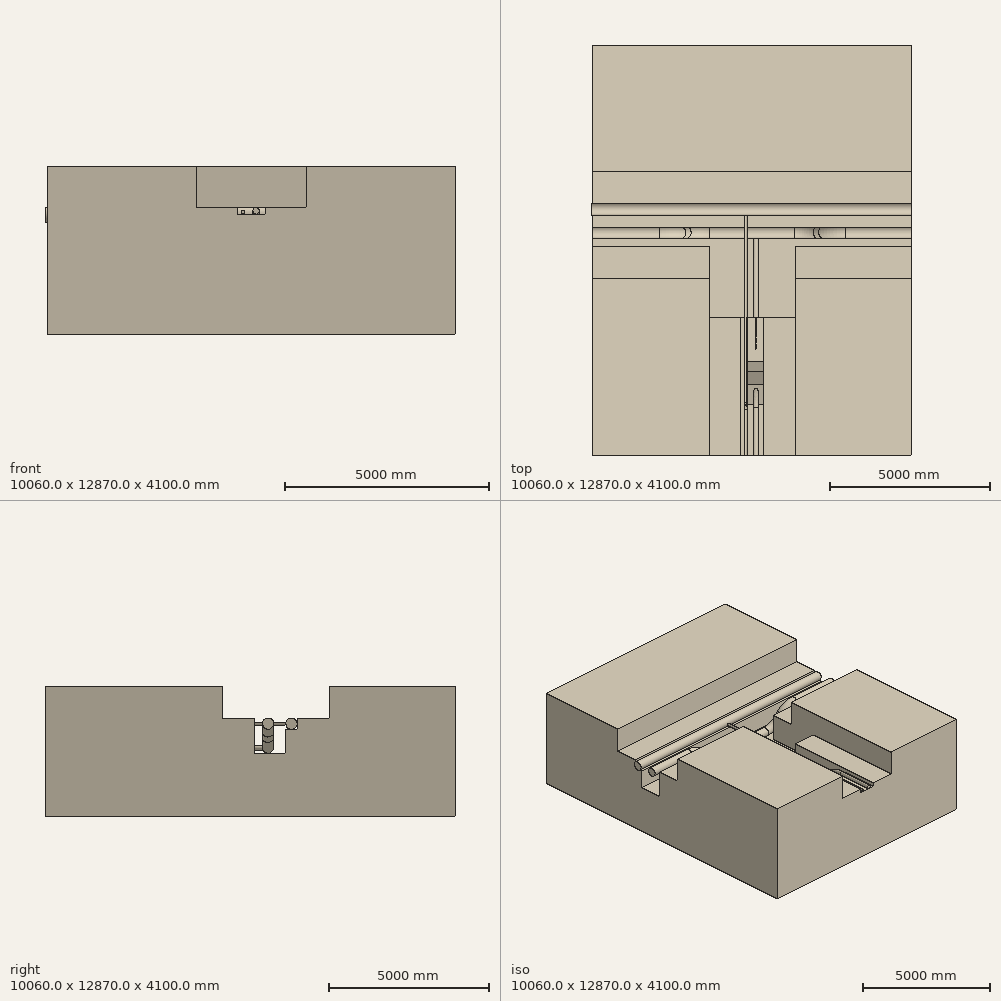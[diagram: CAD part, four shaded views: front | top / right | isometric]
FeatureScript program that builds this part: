
annotation { "Feature Type Name" : "Feature", "Feature Type Description" : "" }
export const myFeature = defineFeature(function(context is Context, id is Id, definition is map)
    precondition{}
    {
        {
            var Q0;
            Q0=qCreatedBy(makeId("Top.planeOp"),FACE);
            var sketch = newSketch(context, id + "F0", { "sketchPlane" : qUnion([Q0])});
            skLineSegment(sketch, "E0.bottom", {"start": v(-4998.89, 4864.79) * mm, "end": v(5001.11, 4864.79) * mm});
            skLineSegment(sketch, "E0.top", {"start": v(-4998.89, -4135.21) * mm, "end": v(5001.11, -4135.21) * mm});
            skLineSegment(sketch, "E0.left", {"start": v(-4998.89, 4864.79) * mm, "end": v(-4998.89, -4135.21) * mm});
            skLineSegment(sketch, "E0.right", {"start": v(5001.11, 4864.79) * mm, "end": v(5001.11, -4135.21) * mm});
            skSolve(sketch);
        }
        {
            var Q0;
            Q0 = qSketchRegion(id + "F0", true);
            extrude(context, id + "F1", {"entities" : qUnion([Q0]), "oppositeDirection" : true, "depth" : 4100 * mm});
        }
        {
            var Q0;
            Q0=makeQuery(id+"F1.opExtrude","SWEPT_FACE",FACE,{"disambiguationData":[OSD([sQuery(id+"F0.wireOp",EDGE,"E0.right")])]});
            var sketch = newSketch(context, id + "F2", { "sketchPlane" : qUnion([Q0])});
            skLineSegment(sketch, "E1", {"start": v(4764.79, 0) * mm, "end": v(4764.79, -1000) * mm});
            skLineSegment(sketch, "E2", {"start": v(4764.79, -1000) * mm, "end": v(3764.79, -1000) * mm});
            skLineSegment(sketch, "E3", {"start": v(3764.79, -1000) * mm, "end": v(3764.79, -1355) * mm});
            skLineSegment(sketch, "E4", {"start": v(3764.79, -1355) * mm, "end": v(3409.79, -1355) * mm});
            skLineSegment(sketch, "E5", {"start": v(2409.79, 0) * mm, "end": v(4764.79, 0) * mm});
            skLineSegment(sketch, "E6", {"start": v(3409.79, -1355) * mm, "end": v(3409.79, -2110) * mm});
            skLineSegment(sketch, "E7", {"start": v(3409.79, -2110) * mm, "end": v(2409.79, -2110) * mm});
            skLineSegment(sketch, "E8", {"start": v(2409.79, -2110) * mm, "end": v(2409.79, 0) * mm});
            skSolve(sketch);
        }
        {
            var Q0;
            Q0 = qSketchRegion(id + "F2", true);
            extrude(context, id + "F3", {"entities" : qUnion([Q0]), "operationType" : NewBodyOperationType.REMOVE, "endBound" : BoundingType.THROUGH_ALL, "oppositeDirection" : true, "depth" : 25 * mm});
        }
        {
            var Q0;
            Q0=makeQuery(id+"F1.opExtrude","SWEPT_FACE",FACE,{"disambiguationData":[OSD([sQuery(id+"F0.wireOp",EDGE,"E0.right")])]});
            var sketch = newSketch(context, id + "F4", { "sketchPlane" : qUnion([Q0])});
            skCircle(sketch, "E9", {"center": v(3587.29, -1177.5) * mm, "radius": 177.5 * mm});
            skSolve(sketch);
        }
        {
            var Q0;
            Q0 = qSketchRegion(id + "F4", true);
            extrude(context, id + "F5", {"entities" : qUnion([Q0]), "operationType" : NewBodyOperationType.ADD, "oppositeDirection" : true, "depth" : 10050 * mm});
        }
        {
            var Q0;
            Q0=makeQuery(id+"F1.opExtrude","SWEPT_FACE",FACE,{"disambiguationData":[OSD([sQuery(id+"F0.wireOp",EDGE,"E0.top")])]});
            var sketch = newSketch(context, id + "F6", { "sketchPlane" : qUnion([Q0])});
            skLineSegment(sketch, "E10.bottom", {"start": v(-348.89, 0) * mm, "end": v(351.11, 0) * mm});
            skLineSegment(sketch, "E10.top", {"start": v(-348.89, -1160) * mm, "end": v(351.11, -1160) * mm});
            skLineSegment(sketch, "E10.left", {"start": v(-348.89, 0) * mm, "end": v(-348.89, -1160) * mm});
            skLineSegment(sketch, "E10.right", {"start": v(351.11, 0) * mm, "end": v(351.11, -1160) * mm});
            skSolve(sketch);
        }
        {
            var Q0;
            Q0 = qSketchRegion(id + "F6", true);
            extrude(context, id + "F7", {"entities" : qUnion([Q0]), "operationType" : NewBodyOperationType.REMOVE, "endBound" : BoundingType.UP_TO_NEXT, "oppositeDirection" : true, "depth" : 25 * mm});
        }
        {
            var Q0;
            Q0=makeQuery(id+"F3.boolean.opBoolean","COPY",FACE,{"derivedFrom":makeQuery(id+"F3.opExtrude","SWEPT_FACE",FACE,{"disambiguationData":[OSD([sQuery(id+"F2.wireOp",EDGE,"E6")])]})});
            cPlane(context, id + "F8", {"entities" : qUnion([Q0]), "cplaneType" : CPlaneType.OFFSET, "offset" : 555 * mm, "width" : 150 * mm, "height" : 150 * mm});
        }
        {
            var Q0;
            Q0=qCreatedBy(id+"F8.planeOp",FACE);
            var sketch = newSketch(context, id + "F9", { "sketchPlane" : qUnion([Q0])});
            skLineSegment(sketch, "E11", {"start": v(-4998.89, -1177.5) * mm, "end": v(-2913.1, -1177.5) * mm});
            skLineSegment(sketch, "E12", {"start": v(-2206, -1470.4) * mm, "end": v(-2036.78, -1639.6) * mm});
            skLineSegment(sketch, "E13", {"start": v(-1329.67, -1932.5) * mm, "end": v(1341.9, -1932.5) * mm});
            skLineSegment(sketch, "E14", {"start": v(2049, -1639.6) * mm, "end": v(2218.22, -1470.4) * mm});
            skLineSegment(sketch, "E15", {"start": v(2925.33, -1177.5) * mm, "end": v(5011.11, -1177.5) * mm});
            skPoint(sketch, "E16.visualSharp", {"position": v(2511.11, -1177.5) * mm});
            skArc(sketch, "E16.filletArc", {"start": v(2925.33, -1177.5) * mm, "mid": v(2542.64, -1253.62) * mm, "end": v(2218.22, -1470.4) * mm});
            skPoint(sketch, "E17.visualSharp", {"position": v(1756.11, -1932.5) * mm});
            skArc(sketch, "E17.filletArc", {"start": v(1341.9, -1932.5) * mm, "mid": v(1724.58, -1856.38) * mm, "end": v(2049, -1639.6) * mm});
            skPoint(sketch, "E18.visualSharp", {"position": v(-1743.89, -1932.5) * mm});
            skArc(sketch, "E18.filletArc", {"start": v(-2036.78, -1639.6) * mm, "mid": v(-1712.36, -1856.38) * mm, "end": v(-1329.67, -1932.5) * mm});
            skPoint(sketch, "E19.visualSharp", {"position": v(-2498.89, -1177.5) * mm});
            skArc(sketch, "E19.filletArc", {"start": v(-2206, -1470.4) * mm, "mid": v(-2530.42, -1253.62) * mm, "end": v(-2913.1, -1177.5) * mm});
            skSolve(sketch);
        }
        {
            var Q0;
            Q0=makeQuery(id+"F1.opExtrude","SWEPT_FACE",FACE,{"disambiguationData":[OSD([sQuery(id+"F0.wireOp",EDGE,"E0.right")])]});
            var sketch = newSketch(context, id + "F10", { "sketchPlane" : qUnion([Q0])});
            skCircle(sketch, "E20", {"center": v(2854.79, -1177.5) * mm, "radius": 177.5 * mm});
            skSolve(sketch);
        }
        {
            var Q0;
            Q0=makeQuery(id+"F10.imprint","IMPRINT",FACE,{"disambiguationData":[TD([[makeQuery(id+"F10.imprint","IMPRINT",EDGE,{"derivedFrom":sQuery(id+"F10.wireOp",EDGE,"E20")}),1.0]])]});
            var Q1;
            Q1 = qConstructionFilter(qBodyType(qCreatedBy(id + "F9" ,EDGE), BodyType.WIRE), ConstructionObject.NO);
            sweep(context, id + "F11", {"profiles" : qUnion([Q0]), "path" : qUnion([Q1])});
        }
        {
            var Q0;
            {var subQ0=sQuery(id+"F0.wireOp",EDGE,"E0.top");var subQ1=makeQuery(id+"F1.opExtrude","SWEPT_FACE",FACE,{"disambiguationData":[OSD([subQ0])]});var subQ2=sQuery(id+"F0.wireOp",EDGE,"E0.right");var subQ3=makeQuery(id+"F1.opExtrude","SWEPT_FACE",FACE,{"disambiguationData":[OSD([subQ2])]});var subQ5=sQuery(id+"F0.wireOp",EDGE,"E0.left");Q0=makeQuery(id+"F7.boolean.opBoolean","SPLIT",FACE,{"disambiguationData":[TD([subQ3])],"derivedFrom":makeQuery(id+"F3.boolean.opBoolean","SPLIT",FACE,{"disambiguationData":[TD([subQ1])],"derivedFrom":makeQuery(id+"F1.opExtrude","CAP_FACE",FACE,{"disambiguationData":[OSD([sQuery(id+"F0.wireOp",EDGE,"E0.bottom"),subQ0,subQ5,subQ2])],"isStart":true})})});}
            var sketch = newSketch(context, id + "F12", { "sketchPlane" : qUnion([Q0])});
            skLineSegment(sketch, "E21.bottom", {"start": v(-1348.89, 2409.79) * mm, "end": v(1351.11, 2409.79) * mm});
            skLineSegment(sketch, "E21.top", {"start": v(-1348.89, 209.79) * mm, "end": v(1351.11, 209.79) * mm});
            skLineSegment(sketch, "E21.left", {"start": v(-1348.89, 2409.79) * mm, "end": v(-1348.89, 209.79) * mm});
            skLineSegment(sketch, "E21.right", {"start": v(1351.11, 2409.79) * mm, "end": v(1351.11, 209.79) * mm});
            skSolve(sketch);
        }
        {
            var Q0;
            Q0 = qSketchRegion(id + "F12", true);
            var Q1;
            Q1=makeQuery(id+"F3.boolean.opBoolean","COPY",FACE,{"derivedFrom":makeQuery(id+"F3.opExtrude","SWEPT_FACE",FACE,{"disambiguationData":[OSD([sQuery(id+"F2.wireOp",EDGE,"E7")])]})});
            extrude(context, id + "F13", {"entities" : qUnion([Q0]), "operationType" : NewBodyOperationType.REMOVE, "endBound" : BoundingType.UP_TO_SURFACE, "oppositeDirection" : true, "endBoundEntityFace" : qUnion([Q1]), "depth" : 25 * mm});
        }
        {
            var Q0;
            {var subQ0=sQuery(id+"F0.wireOp",EDGE,"E0.top");var subQ1=makeQuery(id+"F1.opExtrude","SWEPT_FACE",FACE,{"disambiguationData":[OSD([subQ0])]});var subQ2=sQuery(id+"F0.wireOp",EDGE,"E0.right");var subQ3=makeQuery(id+"F1.opExtrude","SWEPT_FACE",FACE,{"disambiguationData":[OSD([subQ2])]});var subQ5=sQuery(id+"F0.wireOp",EDGE,"E0.left");Q0=makeQuery(id+"F7.boolean.opBoolean","SPLIT",FACE,{"disambiguationData":[TD([subQ3])],"derivedFrom":makeQuery(id+"F3.boolean.opBoolean","SPLIT",FACE,{"disambiguationData":[TD([subQ1])],"derivedFrom":makeQuery(id+"F1.opExtrude","CAP_FACE",FACE,{"disambiguationData":[OSD([sQuery(id+"F0.wireOp",EDGE,"E0.bottom"),subQ0,subQ5,subQ2])],"isStart":true})})});}
            var sketch = newSketch(context, id + "F14", { "sketchPlane" : qUnion([Q0])});
            skLineSegment(sketch, "E22", {"start": v(351.11, 209.79) * mm, "end": v(1351.11, 209.79) * mm});
            skLineSegment(sketch, "E23", {"start": v(1351.11, 209.79) * mm, "end": v(1351.11, 2409.79) * mm});
            skLineSegment(sketch, "E24", {"start": v(1351.11, 2409.79) * mm, "end": v(5001.11, 2409.79) * mm});
            skLineSegment(sketch, "E25", {"start": v(5001.11, 2409.79) * mm, "end": v(5001.11, -4135.21) * mm});
            skLineSegment(sketch, "E26", {"start": v(5001.11, -4135.21) * mm, "end": v(351.11, -4135.21) * mm});
            skLineSegment(sketch, "E27", {"start": v(351.11, -4135.21) * mm, "end": v(351.11, 209.79) * mm});
            skSolve(sketch);
        }
        {
            var Q0;
            Q0 = qSketchRegion(id + "F14", true);
            var Q1;
            {var subQ0=sQuery(id+"F2.wireOp",EDGE,"E7");Q1=makeQuery(id+"F13.boolean.opBoolean","MERGE",FACE,{"derivedFrom":[makeQuery(id+"F3.boolean.opBoolean","COPY",FACE,{"derivedFrom":makeQuery(id+"F3.opExtrude","SWEPT_FACE",FACE,{"disambiguationData":[OSD([subQ0])]})}),makeQuery(id+"F13.opExtrude","CAP_FACE",FACE,{"disambiguationData":[OSD([subQ0])],"isStart":false})]});}
            extrude(context, id + "F15", {"entities" : qUnion([Q0]), "operationType" : NewBodyOperationType.REMOVE, "endBound" : BoundingType.UP_TO_SURFACE, "oppositeDirection" : true, "endBoundEntityFace" : qUnion([Q1]), "depth" : 25 * mm});
        }
        {
            var Q0;
            Q0=makeQuery(id+"F15.boolean.opBoolean","COPY",FACE,{"derivedFrom":makeQuery(id+"F15.opExtrude","SWEPT_FACE",FACE,{"disambiguationData":[OSD([sQuery(id+"F14.wireOp",EDGE,"E27")])]})});
            cPlane(context, id + "F16", {"entities" : qUnion([Q0]), "cplaneType" : CPlaneType.OFFSET, "offset" : (150 + 80) * mm, "oppositeDirection" : true, "width" : 150 * mm, "height" : 150 * mm});
        }
        {
            var Q0;
            Q0=qCreatedBy(id+"F16.planeOp",FACE);
            var sketch = newSketch(context, id + "F17", { "sketchPlane" : qUnion([Q0])});
            skLineSegment(sketch, "E28", {"start": v(-4135.21, -1080) * mm, "end": v(-2632.27, -1080) * mm});
            skLineSegment(sketch, "E29", {"start": v(-1783.74, -1431.47) * mm, "end": v(-1634.19, -1581.03) * mm});
            skLineSegment(sketch, "E30", {"start": v(-785.66, -1932.5) * mm, "end": v(2677.29, -1932.5) * mm});
            skPoint(sketch, "E31.visualSharp", {"position": v(-2135.21, -1080) * mm});
            skArc(sketch, "E31.filletArc", {"start": v(-1783.74, -1431.47) * mm, "mid": v(-2173.05, -1171.34) * mm, "end": v(-2632.27, -1080) * mm});
            skPoint(sketch, "E32.visualSharp", {"position": v(-1282.71, -1932.5) * mm});
            skArc(sketch, "E32.filletArc", {"start": v(-1634.19, -1581.03) * mm, "mid": v(-1244.88, -1841.16) * mm, "end": v(-785.66, -1932.5) * mm});
            skSolve(sketch);
        }
        {
            var Q0;
            Q0=makeQuery(id+"F1.opExtrude","SWEPT_FACE",FACE,{"disambiguationData":[OSD([sQuery(id+"F0.wireOp",EDGE,"E0.top")])]});
            var sketch = newSketch(context, id + "F18", { "sketchPlane" : qUnion([Q0])});
            skCircle(sketch, "E33", {"center": v(121.11, -1080) * mm, "radius": 80 * mm});
            skSolve(sketch);
        }
        {
            var Q0;
            Q0 = qSketchRegion(id + "F18", true);
            var Q1;
            Q1 = qConstructionFilter(qBodyType(qCreatedBy(id + "F17" ,EDGE), BodyType.WIRE), ConstructionObject.NO);
            sweep(context, id + "F19", {"profiles" : qUnion([Q0]), "path" : qUnion([Q1]), "keepProfileOrientation" : true});
        }
        {
            var Q0;
            Q0=makeQuery(id+"F15.boolean.opBoolean","COPY",FACE,{"derivedFrom":makeQuery(id+"F15.opExtrude","SWEPT_FACE",FACE,{"disambiguationData":[OSD([sQuery(id+"F14.wireOp",EDGE,"E27")])]})});
            var sketch = newSketch(context, id + "F20", { "sketchPlane" : qUnion([Q0])});
            skLineSegment(sketch, "E34", {"start": v(-2536.1, -1160) * mm, "end": v(209.79, -1160) * mm});
            skLineSegment(sketch, "E35", {"start": v(209.79, -1160) * mm, "end": v(209.79, -2009.53) * mm});
            skLineSegment(sketch, "E36", {"start": v(209.79, -2009.53) * mm, "end": v(-1197.47, -2009.53) * mm});
            skLineSegment(sketch, "E37", {"start": v(-1197.47, -2009.53) * mm, "end": v(-1504.49, -1799.78) * mm});
            skLineSegment(sketch, "E38", {"start": v(-1504.49, -1799.78) * mm, "end": v(-1901.8, -1426.55) * mm});
            skLineSegment(sketch, "E39", {"start": v(-1901.8, -1426.55) * mm, "end": v(-2536.1, -1160) * mm});
            skSolve(sketch);
        }
        {
            var Q0;
            Q0 = qSketchRegion(id + "F20", true);
            var Q1;
            Q1=makeQuery(id+"F1.opExtrude","SWEPT_BODY",BODY,{"disambiguationData":[OSD([sQuery(id+"F0.wireOp",EDGE,"E0.bottom"),sQuery(id+"F0.wireOp",EDGE,"E0.top"),sQuery(id+"F0.wireOp",EDGE,"E0.left"),sQuery(id+"F0.wireOp",EDGE,"E0.right")])]});
            extrude(context, id + "F21", {"entities" : qUnion([Q0]), "operationType" : NewBodyOperationType.REMOVE, "oppositeDirection" : true, "endBoundEntityBody" : qUnion([Q1]), "depth" : (150 + 160 + 200) * mm});
        }
        {
            var Q0;
            Q0=makeQuery(id+"F1.opExtrude","SWEPT_FACE",FACE,{"disambiguationData":[OSD([sQuery(id+"F0.wireOp",EDGE,"E0.top")])]});
            var sketch = newSketch(context, id + "F22", { "sketchPlane" : qUnion([Q0])});
            skCircle(sketch, "E40", {"center": v(-203.89, -1115) * mm, "radius": 45 * mm});
            skSolve(sketch);
        }
        {
            var Q0;
            Q0=makeQuery(id+"F7.boolean.opBoolean","COPY",FACE,{"derivedFrom":makeQuery(id+"F7.opExtrude","SWEPT_FACE",FACE,{"disambiguationData":[OSD([sQuery(id+"F6.wireOp",EDGE,"E10.left")])]})});
            cPlane(context, id + "F23", {"entities" : qUnion([Q0]), "cplaneType" : CPlaneType.OFFSET, "offset" : (100 + 45) * mm, "width" : 150 * mm, "height" : 150 * mm});
        }
        {
            var Q0;
            Q0=qCreatedBy(id+"F23.planeOp",FACE);
            var sketch = newSketch(context, id + "F24", { "sketchPlane" : qUnion([Q0])});
            skLineSegment(sketch, "E41", {"start": v(-4135.21, -1115) * mm, "end": v(-2682.1, -1115) * mm});
            skLineSegment(sketch, "E42", {"start": v(-2594.6, -1138.45) * mm, "end": v(-2567.57, -1154.05) * mm});
            skLineSegment(sketch, "E43", {"start": v(-2480.07, -1177.5) * mm, "end": v(3409.79, -1177.5) * mm});
            skPoint(sketch, "E44.visualSharp", {"position": v(-2635.21, -1115) * mm});
            skArc(sketch, "E44.filletArc", {"start": v(-2594.6, -1138.45) * mm, "mid": v(-2636.81, -1120.96) * mm, "end": v(-2682.1, -1115) * mm});
            skPoint(sketch, "E45.visualSharp", {"position": v(-2526.96, -1177.5) * mm});
            skArc(sketch, "E45.filletArc", {"start": v(-2567.57, -1154.05) * mm, "mid": v(-2525.36, -1171.54) * mm, "end": v(-2480.07, -1177.5) * mm});
            skSolve(sketch);
        }
        {
            var Q0;
            Q0=makeQuery(id+"F22.imprint","IMPRINT",FACE,{"disambiguationData":[TD([[makeQuery(id+"F22.imprint","IMPRINT",EDGE,{"derivedFrom":sQuery(id+"F22.wireOp",EDGE,"E40")}),1.0]])]});
            var Q1;
            Q1 = qConstructionFilter(qBodyType(qCreatedBy(id + "F24" ,EDGE), BodyType.WIRE), ConstructionObject.NO);
            sweep(context, id + "F25", {"profiles" : qUnion([Q0]), "path" : qUnion([Q1])});
        }
        {
            var Q0;
            {var subQ0=sQuery(id+"F2.wireOp",EDGE,"E7");Q0=makeQuery(id+"F15.boolean.opBoolean","MERGE",FACE,{"derivedFrom":[makeQuery(id+"F13.boolean.opBoolean","MERGE",FACE,{"derivedFrom":[makeQuery(id+"F3.boolean.opBoolean","COPY",FACE,{"derivedFrom":makeQuery(id+"F3.opExtrude","SWEPT_FACE",FACE,{"disambiguationData":[OSD([subQ0])]})}),makeQuery(id+"F13.opExtrude","CAP_FACE",FACE,{"disambiguationData":[OSD([subQ0])],"isStart":false})]}),makeQuery(id+"F15.opExtrude","CAP_FACE",FACE,{"disambiguationData":[OSD([subQ0])],"isStart":false})]});}
            var sketch = newSketch(context, id + "F26", { "sketchPlane" : qUnion([Q0])});
            skLineSegment(sketch, "E46", {"start": v(5001.11, -4135.21) * mm, "end": v(351.11, -4135.21) * mm});
            skLineSegment(sketch, "E47", {"start": v(351.11, -4135.21) * mm, "end": v(351.11, 209.79) * mm});
            skLineSegment(sketch, "E48", {"start": v(351.11, 209.79) * mm, "end": v(1351.11, 209.79) * mm});
            skLineSegment(sketch, "E49", {"start": v(1351.11, 209.79) * mm, "end": v(1351.11, 2409.79) * mm});
            skLineSegment(sketch, "E50", {"start": v(1351.11, 2409.79) * mm, "end": v(5001.11, 2409.79) * mm});
            skLineSegment(sketch, "E51", {"start": v(5001.11, 2409.79) * mm, "end": v(5001.11, -4135.21) * mm});
            skSolve(sketch);
        }
        {
            var Q0;
            Q0 = qSketchRegion(id + "F26", true);
            var Q1;
            {var subQ0=sQuery(id+"F0.wireOp",EDGE,"E0.top");var subQ1=makeQuery(id+"F1.opExtrude","SWEPT_FACE",FACE,{"disambiguationData":[OSD([subQ0])]});var subQ2=sQuery(id+"F0.wireOp",EDGE,"E0.left");var subQ3=makeQuery(id+"F1.opExtrude","SWEPT_FACE",FACE,{"disambiguationData":[OSD([subQ2])]});var subQ5=sQuery(id+"F0.wireOp",EDGE,"E0.right");Q1=makeQuery(id+"F7.boolean.opBoolean","SPLIT",FACE,{"disambiguationData":[TD([subQ3])],"derivedFrom":makeQuery(id+"F3.boolean.opBoolean","SPLIT",FACE,{"disambiguationData":[TD([subQ1])],"derivedFrom":makeQuery(id+"F1.opExtrude","CAP_FACE",FACE,{"disambiguationData":[OSD([sQuery(id+"F0.wireOp",EDGE,"E0.bottom"),subQ0,subQ2,subQ5])],"isStart":true})})});}
            extrude(context, id + "F27", {"entities" : qUnion([Q0]), "operationType" : NewBodyOperationType.ADD, "endBound" : BoundingType.UP_TO_SURFACE, "endBoundEntityFace" : qUnion([Q1]), "depth" : 25 * mm});
        }
        {
            var Q0;
            Q0=makeQuery(id+"F27.opExtrude","CAP_FACE",FACE,{"disambiguationData":[OSD([sQuery(id+"F26.wireOp",EDGE,"E46"),sQuery(id+"F26.wireOp",EDGE,"E47"),sQuery(id+"F26.wireOp",EDGE,"E48"),sQuery(id+"F26.wireOp",EDGE,"E49"),sQuery(id+"F26.wireOp",EDGE,"E50"),sQuery(id+"F26.wireOp",EDGE,"E51")])],"isStart":false});
            var sketch = newSketch(context, id + "F28", { "sketchPlane" : qUnion([Q0])});
            skLineSegment(sketch, "E52.bottom", {"start": v(5001.11, 2409.79) * mm, "end": v(1351.11, 2409.79) * mm});
            skLineSegment(sketch, "E52.top", {"start": v(5001.11, 1409.79) * mm, "end": v(1351.11, 1409.79) * mm});
            skLineSegment(sketch, "E52.left", {"start": v(5001.11, 2409.79) * mm, "end": v(5001.11, 1409.79) * mm});
            skLineSegment(sketch, "E52.right", {"start": v(1351.11, 2409.79) * mm, "end": v(1351.11, 1409.79) * mm});
            skLineSegment(sketch, "E53.bottom", {"start": v(351.11, 209.79) * mm, "end": v(1351.11, 209.79) * mm});
            skLineSegment(sketch, "E53.top", {"start": v(351.11, -4135.21) * mm, "end": v(1351.11, -4135.21) * mm});
            skLineSegment(sketch, "E53.left", {"start": v(351.11, 209.79) * mm, "end": v(351.11, -4135.21) * mm});
            skLineSegment(sketch, "E53.right", {"start": v(1351.11, 209.79) * mm, "end": v(1351.11, -4135.21) * mm});
            skSolve(sketch);
        }
        {
            var Q0;
            Q0 = qSketchRegion(id + "F28", true);
            extrude(context, id + "F29", {"entities" : qUnion([Q0]), "operationType" : NewBodyOperationType.REMOVE, "oppositeDirection" : true, "depth" : 1000 * mm});
        }
        {
            var Q0;
            {var subQ0=sQuery(id+"F0.wireOp",EDGE,"E0.top");var subQ1=makeQuery(id+"F1.opExtrude","SWEPT_FACE",FACE,{"disambiguationData":[OSD([subQ0])]});var subQ2=sQuery(id+"F0.wireOp",EDGE,"E0.left");var subQ3=makeQuery(id+"F1.opExtrude","SWEPT_FACE",FACE,{"disambiguationData":[OSD([subQ2])]});var subQ5=sQuery(id+"F0.wireOp",EDGE,"E0.right");Q0=makeQuery(id+"F7.boolean.opBoolean","SPLIT",FACE,{"disambiguationData":[TD([subQ3])],"derivedFrom":makeQuery(id+"F3.boolean.opBoolean","SPLIT",FACE,{"disambiguationData":[TD([subQ1])],"derivedFrom":makeQuery(id+"F1.opExtrude","CAP_FACE",FACE,{"disambiguationData":[OSD([sQuery(id+"F0.wireOp",EDGE,"E0.bottom"),subQ0,subQ2,subQ5])],"isStart":true})})});}
            var sketch = newSketch(context, id + "F30", { "sketchPlane" : qUnion([Q0])});
            skLineSegment(sketch, "E54.bottom", {"start": v(-4998.89, 2409.79) * mm, "end": v(-1348.89, 2409.79) * mm});
            skLineSegment(sketch, "E54.top", {"start": v(-4998.89, 1409.79) * mm, "end": v(-1348.89, 1409.79) * mm});
            skLineSegment(sketch, "E54.left", {"start": v(-4998.89, 2409.79) * mm, "end": v(-4998.89, 1409.79) * mm});
            skLineSegment(sketch, "E54.right", {"start": v(-1348.89, 2409.79) * mm, "end": v(-1348.89, 1409.79) * mm});
            skLineSegment(sketch, "E55.bottom", {"start": v(-348.89, -4135.21) * mm, "end": v(-1348.89, -4135.21) * mm});
            skLineSegment(sketch, "E55.top", {"start": v(-348.89, 209.79) * mm, "end": v(-1348.89, 209.79) * mm});
            skLineSegment(sketch, "E55.left", {"start": v(-348.89, -4135.21) * mm, "end": v(-348.89, 209.79) * mm});
            skLineSegment(sketch, "E55.right", {"start": v(-1348.89, -4135.21) * mm, "end": v(-1348.89, 209.79) * mm});
            skSolve(sketch);
        }
        {
            var Q0;
            Q0 = qSketchRegion(id + "F30", true);
            extrude(context, id + "F31", {"entities" : qUnion([Q0]), "operationType" : NewBodyOperationType.REMOVE, "oppositeDirection" : true, "depth" : 1000 * mm});
        }
        {
            var Q0;
            Q0=makeQuery(id+"F1.opExtrude","SWEPT_FACE",FACE,{"disambiguationData":[OSD([sQuery(id+"F0.wireOp",EDGE,"E0.bottom")])]});
            var sketch = newSketch(context, id + "F32", { "sketchPlane" : qUnion([Q0])});
            skLineSegment(sketch, "E56.bottom", {"start": v(-5001.11, 0) * mm, "end": v(4998.89, 0) * mm});
            skLineSegment(sketch, "E56.top", {"start": v(-5001.11, -4100) * mm, "end": v(4998.89, -4100) * mm});
            skLineSegment(sketch, "E56.left", {"start": v(-5001.11, 0) * mm, "end": v(-5001.11, -4100) * mm});
            skLineSegment(sketch, "E56.right", {"start": v(4998.89, 0) * mm, "end": v(4998.89, -4100) * mm});
            skSolve(sketch);
        }
        {
            var Q0;
            Q0 = qSketchRegion(id + "F32", true);
            extrude(context, id + "F33", {"entities" : qUnion([Q0]), "operationType" : NewBodyOperationType.ADD, "depth" : 3870 * mm});
        }
    });
